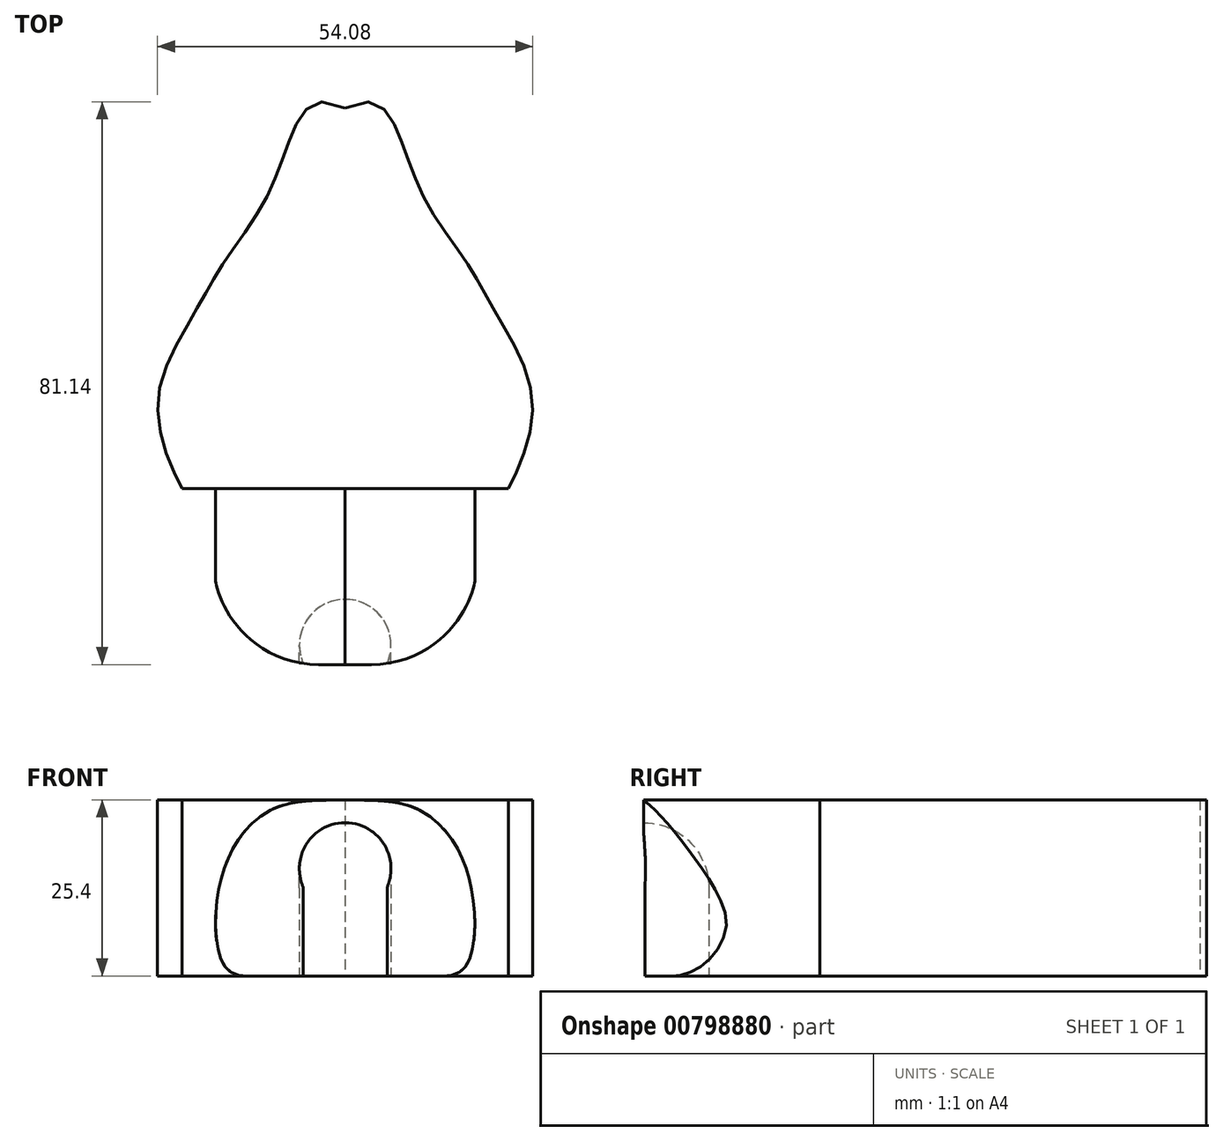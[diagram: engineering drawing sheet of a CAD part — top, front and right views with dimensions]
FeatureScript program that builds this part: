
annotation { "Feature Type Name" : "Feature", "Feature Type Description" : "" }
export const myFeature = defineFeature(function(context is Context, id is Id, definition is map)
    precondition{}
    {
        {
            var Q0;
            Q0=qCreatedBy(makeId("Top.planeOp"),FACE);
            var sketch = newSketch(context, id + "F0", { "sketchPlane" : qUnion([Q0])});
            skLineSegment(sketch, "E0.top", {"start": v(-3.81, -50.8) * mm, "end": v(3.81, -50.8) * mm});
            skLineSegment(sketch, "E0.right", {"start": v(19.05, -35.56) * mm, "end": v(19.05, -35.56) * mm});
            skPoint(sketch, "E1", {"position": v(19.05, -35.56) * mm});
            skPoint(sketch, "E2", {"position": v(0, 0) * mm});
            skLineSegment(sketch, "E3", {"start": v(0, 0) * mm, "end": v(0, -50.8) * mm, "construction": true});
            skFitSpline(sketch, "E4", {"points": [v(19.05, -35.56) * mm, v(21.16, -29.63) * mm, v(24, -24.5) * mm, v(26.99, -12.58) * mm, v(21.66, 0) * mm, v(17.66, 6.94) * mm, v(11.34, 16.54) * mm, v(7.4, 26.36) * mm, v(0, 29.41) * mm], "startDerivative": vector(4.35, 77.98) * mm, "endDerivative": vector(-114.72, -61.93) * mm});
            skFitSpline(sketch, "E5.MirrorCS", {"points": [v(-19.05, -35.56) * mm, v(-21.16, -29.63) * mm, v(-24, -24.5) * mm, v(-26.99, -12.58) * mm, v(-21.66, 0) * mm, v(-17.66, 6.94) * mm, v(-11.34, 16.54) * mm, v(-7.4, 26.36) * mm, v(0, 29.41) * mm], "startDerivative": vector(-4.35, 77.98) * mm, "endDerivative": vector(114.72, -61.93) * mm});
            skLineSegment(sketch, "E6.MirrorCS", {"start": v(-19.05, -35.56) * mm, "end": v(-19.05, -35.56) * mm});
            skPoint(sketch, "E7.visualSharp", {"position": v(-19.05, -50.8) * mm});
            skArc(sketch, "E7.filletArc", {"start": v(-19.05, -35.56) * mm, "mid": v(-14.59, -46.34) * mm, "end": v(-3.81, -50.8) * mm});
            skPoint(sketch, "E8.visualSharp", {"position": v(19.05, -50.8) * mm});
            skArc(sketch, "E8.filletArc", {"start": v(3.81, -50.8) * mm, "mid": v(14.59, -46.34) * mm, "end": v(19.05, -35.56) * mm});
            skSolve(sketch);
        }
        {
            var Q0;
            Q0=makeQuery(id+"F0.imprint","IMPRINT",FACE,{"disambiguationData":[TD([[makeQuery(id+"F0.imprint","IMPRINT",EDGE,{"derivedFrom":sQuery(id+"F0.wireOp",EDGE,"E0.top")}),1.0]])]});
            extrude(context, id + "F1", {"entities" : qUnion([Q0]), "depth" : 25.4 * mm, "offsetDistance" : 25.4 * mm});
        }
        {
            var Q0;
            Q0=makeQuery(id+"F0.imprint","IMPRINT",FACE,{"disambiguationData":[TD([[makeQuery(id+"F0.imprint","IMPRINT",EDGE,{"derivedFrom":sQuery(id+"F0.wireOp",EDGE,"E0.top")}),1.0]])]});
            cPlane(context, id + "F2", {"entities" : qUnion([Q0]), "cplaneType" : CPlaneType.OFFSET, "offset" : 0 * mm, "width" : 152.4 * mm, "height" : 152.4 * mm});
        }
        {
            var Q0;
            Q0=qCreatedBy(id+"F2.planeOp",FACE);
            var sketch = newSketch(context, id + "F3", { "sketchPlane" : qUnion([Q0])});
            skLineSegment(sketch, "E9.bottom", {"start": v(3.81, -48.01) * mm, "end": v(-3.81, -48.01) * mm, "construction": true});
            skLineSegment(sketch, "E9.top", {"start": v(3.8, -55.95) * mm, "end": v(0, -55.95) * mm});
            skLineSegment(sketch, "E9.left", {"start": v(3.8, -48.01) * mm, "end": v(3.8, -53.4) * mm, "construction": true});
            skLineSegment(sketch, "E9.right", {"start": v(-3.81, -48.01) * mm, "end": v(-3.81, -53.4) * mm, "construction": true});
            skPoint(sketch, "E10", {"position": v(0, -55.95) * mm});
            skPoint(sketch, "E10.positionSnap0", {"position": v(0, -55.95) * mm});
            skLineSegment(sketch, "E11", {"start": v(0, -55.95) * mm, "end": v(-3.8, -55.95) * mm});
            skPoint(sketch, "E12", {"position": v(-3.81, -53.4) * mm});
            skPoint(sketch, "E13", {"position": v(3.81, -53.4) * mm});
            skLineSegment(sketch, "E14", {"start": v(-3.81, -53.4) * mm, "end": v(-3.81, -55.95) * mm});
            skLineSegment(sketch, "E15", {"start": v(3.8, -53.4) * mm, "end": v(3.8, -55.95) * mm});
            skArc(sketch, "E16", {"start": v(3.81, -53.4) * mm, "mid": v(0, -41.4) * mm, "end": v(-3.81, -53.4) * mm});
            skArc(sketch, "E17", {"start": v(-3.81, -53.4) * mm, "mid": v(0, -54.62) * mm, "end": v(3.81, -53.4) * mm, "construction": true});
            skLineSegment(sketch, "E18", {"start": v(0, -48.01) * mm, "end": v(5.99, -50.8) * mm, "construction": true});
            skLineSegment(sketch, "E19", {"start": v(0, -48.01) * mm, "end": v(0, -55.95) * mm, "construction": true});
            skLineSegment(sketch, "E20.MirrorCS", {"start": v(0, -48.01) * mm, "end": v(-5.99, -50.8) * mm, "construction": true});
            skLineSegment(sketch, "E21", {"start": v(5.99, -50.8) * mm, "end": v(-5.99, -50.8) * mm, "construction": true});
            skPoint(sketch, "E22", {"position": v(0, -50.8) * mm});
            skSolve(sketch);
        }
        {
            var Q0;
            Q0=makeQuery(id+"F3.imprint","IMPRINT",FACE,{"disambiguationData":[TD([[makeQuery(id+"F3.imprint","IMPRINT",EDGE,{"derivedFrom":sQuery(id+"F3.wireOp",EDGE,"E9.top")}),-1.0]])]});
            extrude(context, id + "F4", {"entities" : qUnion([Q0]), "operationType" : NewBodyOperationType.REMOVE, "depth" : 12.7 * mm, "offsetDistance" : 25.4 * mm});
        }
        {
            var Q0;
            Q0=makeQuery(id+"F4.boolean.opBoolean","COPY",FACE,{"derivedFrom":makeQuery(id+"F4.opExtrude","CAP_FACE",FACE,{"disambiguationData":[OSD([sQuery(id+"F3.wireOp",EDGE,"E9.top"),sQuery(id+"F3.wireOp",EDGE,"E11"),sQuery(id+"F3.wireOp",EDGE,"E14"),sQuery(id+"F3.wireOp",EDGE,"E15"),sQuery(id+"F3.wireOp",EDGE,"E16")])],"isStart":false})});
            cPlane(context, id + "F5", {"entities" : qUnion([Q0]), "cplaneType" : CPlaneType.OFFSET, "offset" : 0 * mm, "width" : 152.4 * mm, "height" : 152.4 * mm});
        }
        {
            var Q0;
            Q0=qCreatedBy(id+"F5.planeOp",FACE);
            var sketch = newSketch(context, id + "F6", { "sketchPlane" : qUnion([Q0])});
            skPoint(sketch, "E23", {"position": v(0, 48.01) * mm});
            skPoint(sketch, "E24", {"position": v(0, 50.8) * mm});
            skLineSegment(sketch, "E25", {"start": v(0, 50.8) * mm, "end": v(5.99, 50.8) * mm});
            skLineSegment(sketch, "E26", {"start": v(0, 50.8) * mm, "end": v(-5.99, 50.8) * mm});
            skArc(sketch, "E27", {"start": v(-5.99, 50.8) * mm, "mid": v(0, 41.4) * mm, "end": v(5.99, 50.8) * mm});
            skSolve(sketch);
        }
        {
            var Q0;
            Q0 = qSketchRegion(id + "F6", true);
            var Q1;
            Q1=makeQuery(id+"F4.boolean.opBoolean","INTERSECT",EDGE,{"derivedFrom":[makeQuery(id+"F1.opExtrude","SWEPT_FACE",FACE,{"disambiguationData":[OSD([sQuery(id+"F0.wireOp",EDGE,"E0.top")])]}),makeQuery(id+"F4.opExtrude","CAP_FACE",FACE,{"disambiguationData":[OSD([sQuery(id+"F3.wireOp",EDGE,"E9.top"),sQuery(id+"F3.wireOp",EDGE,"E11"),sQuery(id+"F3.wireOp",EDGE,"E14"),sQuery(id+"F3.wireOp",EDGE,"E15"),sQuery(id+"F3.wireOp",EDGE,"E16")])],"isStart":false})]});
            revolve(context, id + "F7", {"operationType" : NewBodyOperationType.REMOVE, "surfaceOperationType" : NewSurfaceOperationType.NEW, "entities" : qUnion([Q0]), "axis" : qUnion([Q1]), "revolveType" : RevolveType.ONE_DIRECTION, "angle" : 92 * degree});
        }
        {
            var Q0;
            Q0=makeQuery(id+"F1.opExtrude","SWEPT_FACE",FACE,{"disambiguationData":[OSD([sQuery(id+"F0.wireOp",EDGE,"E0.top")])]});
            cPlane(context, id + "F8", {"entities" : qUnion([Q0]), "cplaneType" : CPlaneType.OFFSET, "offset" : 0 * mm, "width" : 152.4 * mm, "height" : 152.4 * mm});
        }
        {
            var Q0;
            Q0=qCreatedBy(id+"F8.planeOp",FACE);
            var sketch = newSketch(context, id + "F9", { "sketchPlane" : qUnion([Q0])});
            skLineSegment(sketch, "E28", {"start": v(0, 25.4) * mm, "end": v(0, 0) * mm, "construction": true});
            skLineSegment(sketch, "E29", {"start": v(0, 0) * mm, "end": v(-14.08, 0) * mm});
            skFitSpline(sketch, "E30", {"points": [v(-14.08, 0) * mm, v(-18.11, 3) * mm, v(-17.28, 15.93) * mm, v(-10.05, 24.23) * mm, v(0, 25.4) * mm], "startDerivative": vector(-39.28, 0) * mm, "endDerivative": vector(40.82, 1.4) * mm});
            skFitSpline(sketch, "E31.MirrorCS", {"points": [v(14.08, 0) * mm, v(18.11, 3) * mm, v(17.28, 15.93) * mm, v(10.05, 24.23) * mm, v(0, 25.4) * mm], "startDerivative": vector(39.28, 0) * mm, "endDerivative": vector(-40.82, 1.4) * mm});
            skLineSegment(sketch, "E32.MirrorCS", {"start": v(0, 0) * mm, "end": v(14.08, 0) * mm});
            skLineSegment(sketch, "E33.bottom", {"start": v(-34.1, 38.3) * mm, "end": v(37.91, 38.3) * mm});
            skLineSegment(sketch, "E33.top", {"start": v(-34.1, -11.1) * mm, "end": v(37.91, -11.1) * mm});
            skLineSegment(sketch, "E33.left", {"start": v(-34.1, 38.3) * mm, "end": v(-34.1, -11.1) * mm});
            skLineSegment(sketch, "E33.right", {"start": v(37.91, 38.3) * mm, "end": v(37.91, -11.1) * mm});
            skSolve(sketch);
        }
        {
            var Q0;
            Q0 = qSketchRegion(id + "F9", true);
            extrude(context, id + "F10", {"entities" : qUnion([Q0]), "operationType" : NewBodyOperationType.REMOVE, "oppositeDirection" : true, "depth" : 25.4 * mm, "offsetDistance" : 25.4 * mm});
        }
    });
